# Revit family: PRD_FrankeWS_PlstcsBrckts_WallMounting_FAID905
name_source: partatom
category: Plumbing Fixtures
revit_build: Autodesk Revit 2018 (Build: 20190510_1515(x64)
units: mm (PartAtom-declared; Revit-internal decimal feet)

## family parameters
Cut with Voids When Loaded = Yes
Host = Face
OmniClass Number = 23.45.05.14.24
OmniClass Title = Eye Wash Fountains
Part Type = Normal
Room Calculation Point = No
Round Connector Dimension = Use Diameter
Shared = Yes

## types (1)
- FAID905
    AssetType = Fixed
    BIMObjectName = PRD_AR_PlasticsBrackets_WallMounting_FAID905
    Category = Pr_20_85_09_63, Plastics brackets
    Color = white
    Default Elevation = 1500 mm  [stored 4.92126 ft]
    Description = Wall bracket, plastic, white, with screw mounting. Complementary part or spare part for the eye- and face-wash fountains FAID100, FAID101, FAID102, FAID103.
    DurationUnit = year
    Features = plastic, white
    GrossWeight = 0.08 kg
    IfcExportAs = IfcSanitaryTerminalType
    IfcExportType = USERDEFINED
    Manufacturer = KWC Group AG
    ManufacturerName = KWC Group AG
    ManufacturerURL = www.kwc.com
    Material = Plastic
    Model = FAID905
    ModelNumber = 2000103189
    ModelReference = FAID905
    MountingMaterial = PRD_AR_Plastic_White
    Name = Wall mounting FAID905
    NetWeight = 0.08 kg
    NominalDepth = 0 mm  [stored 0 ft]
    NominalHeight = 0 mm  [stored 0 ft]
    NominalLength = 0 mm  [stored 0 ft]
    NominalWidth = 0 mm  [stored 0 ft]
    ProductCode = 230.0639.284
    ProductInformation = https://pim.kwc.com
    Quantity = 1
    QuantityUom = Piece
    Status = New
    TailorMade = No
    URL = www.kwc.com
    Uniclass2015Code = Pr_20_85_09_63
    Uniclass2015Title = Plastics brackets
    Uniclass2015Version = Products v1.17
    Version = 1
    WarrantyDurationUnit = year

note: [stored X ft] marks values corroborated as IEEE doubles in the binary element streams (Revit-internal decimal feet)

## geometry (parser evidence)
native form markers: Sweep x2
no freeform markers — native parametric forms only
